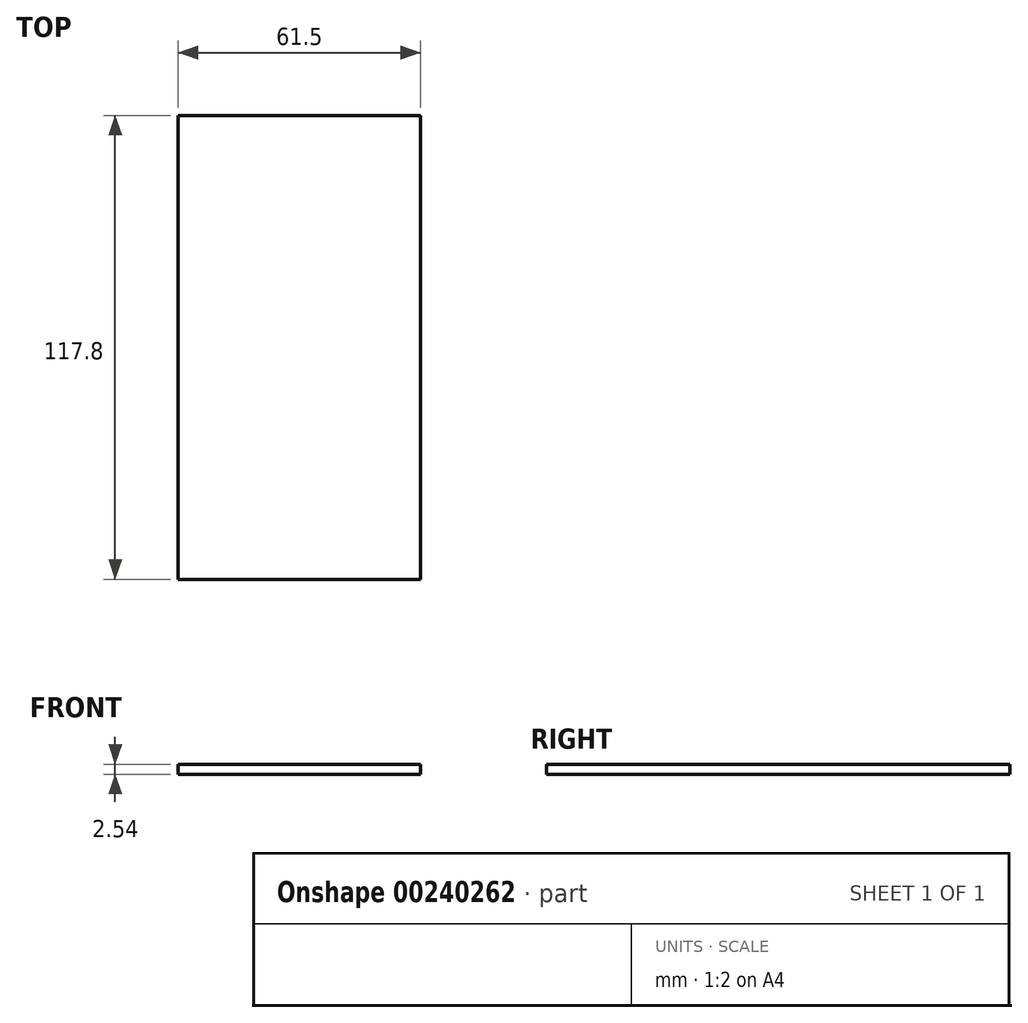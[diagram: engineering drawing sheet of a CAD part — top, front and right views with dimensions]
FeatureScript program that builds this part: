
annotation { "Feature Type Name" : "Feature", "Feature Type Description" : "" }
export const myFeature = defineFeature(function(context is Context, id is Id, definition is map)
    precondition{}
    {
        {
            var Q0;
            Q0=qCreatedBy(makeId("Top.planeOp"),FACE);
            var sketch = newSketch(context, id + "F0", { "sketchPlane" : qUnion([Q0])});
            skLineSegment(sketch, "E0.bottom", {"start": v(44.6, 48.94) * mm, "end": v(-16.89, 48.94) * mm});
            skLineSegment(sketch, "E0.top", {"start": v(44.6, -68.86) * mm, "end": v(-16.89, -68.86) * mm});
            skLineSegment(sketch, "E0.left", {"start": v(44.6, 48.94) * mm, "end": v(44.6, -68.86) * mm});
            skLineSegment(sketch, "E0.right", {"start": v(-16.89, 48.94) * mm, "end": v(-16.89, -68.86) * mm});
            skSolve(sketch);
        }
        {
            var Q0;
            Q0=makeQuery(id+"F0.imprint","IMPRINT",FACE,{"disambiguationData":[TD([[makeQuery(id+"F0.imprint","IMPRINT",EDGE,{"derivedFrom":sQuery(id+"F0.wireOp",EDGE,"E0.bottom")}),1.0]])]});
            extrude(context, id + "F1", {"entities" : qUnion([Q0]), "depth" : 2.54 * mm});
        }
    });
